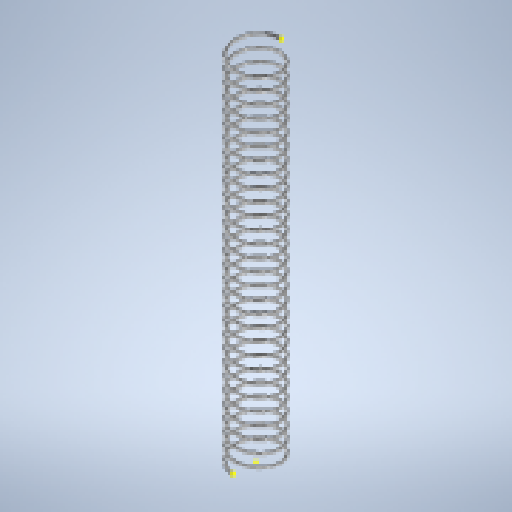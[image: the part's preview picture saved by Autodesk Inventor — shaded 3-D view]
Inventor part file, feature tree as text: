
AUTODESK INVENTOR PART (.ipt)
format: ipt  version: 2025.1 (Build 291241020, 241B)  size: 503,808 bytes
history: native  units: mm
features: sketch x3, plane x2, split x2, helix x1
ambient origin geometry x8: Origin, YZ Plane, XZ Plane, XY Plane, X Axis, Y Axis, Z Axis, Center Point
bodies: Solid1 (feature_tree)
feature tree (8):
  helix  "Coil1"  [1 undecoded]
  sketch  "Sketch2"  dims[d2=5.08mm d3=180.0mm d4=10.0mm d5=0.0mm d6=90.0deg d7=90.0deg d8=0.0mm d9=0.0mm]
  plane  "Work Plane1"
  sketch  "Sketch4"
  plane  "Work Plane2"
  split  "Split1"
  split  "Split2"
  sketch  "Sketch1"  dims[d1=9.4mm]
note: 1 required parameter value undecoded (feature->parameter linkage not recoverable at this tier; creation-order binding heuristic only, values carry confidence <= 0.55)
